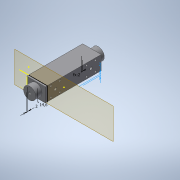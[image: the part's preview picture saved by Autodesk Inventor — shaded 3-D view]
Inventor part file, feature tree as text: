
AUTODESK INVENTOR PART (.ipt)
format: ipt  version: 2020 (Build 240168000, 168)  size: 256,512 bytes
history: native  units: mm
features: extrude x10, sketch x10, reference x9, other x7, projected_geometry x3, hole x1, mirror x1
ambient origin geometry x8: Origin, YZ Plane, XZ Plane, XY Plane, X Axis, Y Axis, Z Axis, Center Point
bodies: Body1 (feature_tree)
feature tree (41):
  other  "Bryła1"
  other  "Płaszczyzna konstrukcyjna1"
  extrude  "Wyciągnięcie proste1"  Depth=3.0mm TaperAngle=0.0deg
  extrude  "Wyciągnięcie proste2"  Depth=6.0mm
  extrude  "Wyciągnięcie proste3"  Depth=20.0mm TaperAngle=0.0deg
  sketch  "Szkic4"
  extrude  "Wyciągnięcie proste4"  Depth=0.25mm
  other  "Płaszczyzna konstrukcyjna2"
  extrude  "Wyciągnięcie proste5"  Depth=0.25mm
  hole  "Otwór3"  [1 undecoded]
  extrude  "Wyciągnięcie proste8"  Depth=0.25mm
  extrude  "Wyciągnięcie proste7"  Depth=20.0mm TaperAngle=0.0deg
  extrude  "Wyciągnięcie proste9"  Depth=14.6mm
  mirror  "Odbij1"
  extrude  "Wyciągnięcie proste10"  TaperAngle=0.0deg  [1 undecoded]
  extrude  "Wyciągnięcie proste11"  Depth=3.0mm TaperAngle=0.0deg
  sketch  "Szkic1"
  reference  "Odniesienie1"
  reference  "Odniesienie2"
  sketch  "Szkic2"
  sketch  "Szkic3"
  reference  "Odniesienie3"
  reference  "Odniesienie4"
  reference  "Odniesienie5"
  reference  "Odniesienie6"
  reference  "Odniesienie7"
  sketch  "Szkic5"
  projected_geometry  "Pętla rzutowana1"
  sketch  "Szkic6"
  sketch  "Szkic7"
  reference  "Odniesienie8"
  reference  "Odniesienie9"
  sketch  "Szkic8"
  projected_geometry  "Pętla rzutowana2"
  sketch  "Szkic9"
  projected_geometry  "Pętla rzutowana3"
  sketch  "Szkic11"
  other  "<userpath>\Desktop\3d\scanning-robot\Assembly1.iam"
  other  "Assembly1.iam"
  other  "wheel-adapter:1"
  other  "wheel:1"
note: 2 required parameter values undecoded (feature->parameter linkage not recoverable at this tier; creation-order binding heuristic only, values carry confidence <= 0.55)
